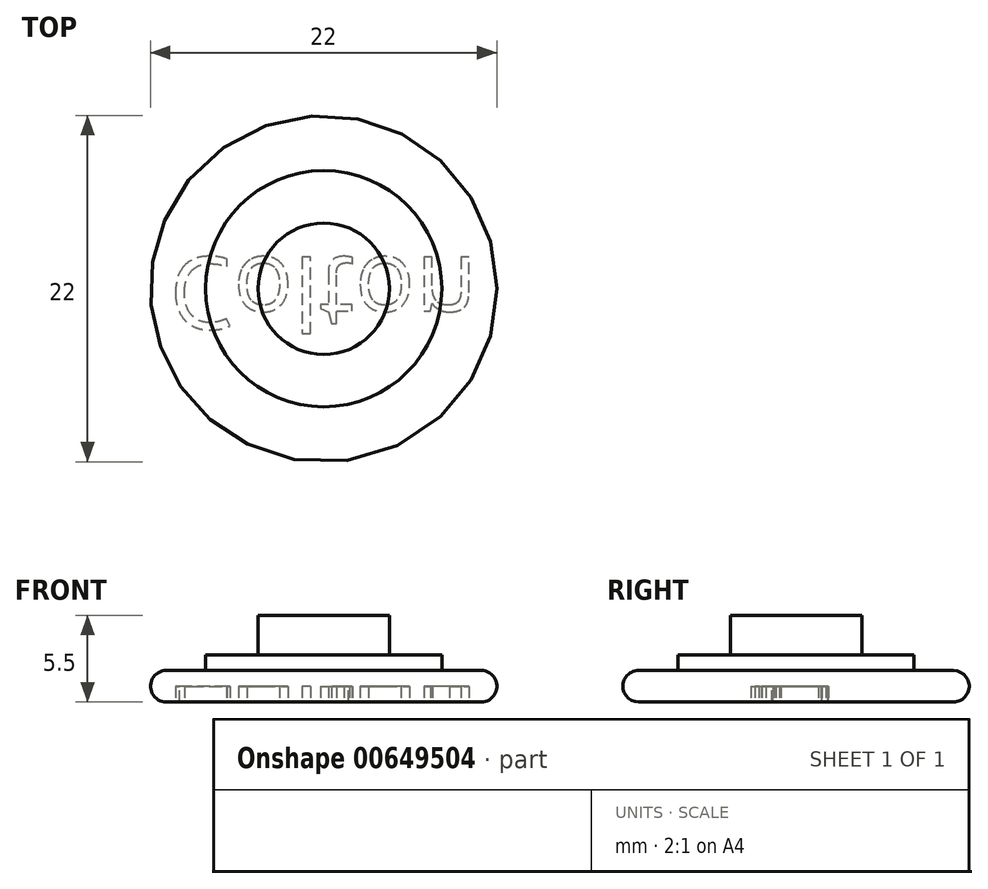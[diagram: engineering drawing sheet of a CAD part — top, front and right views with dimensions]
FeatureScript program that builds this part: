
annotation { "Feature Type Name" : "Feature", "Feature Type Description" : "" }
export const myFeature = defineFeature(function(context is Context, id is Id, definition is map)
    precondition{}
    {
        {
            var Q0;
            Q0=qCreatedBy(makeId("Top.planeOp"),FACE);
            var sketch = newSketch(context, id + "F0", { "sketchPlane" : qUnion([Q0])});
            skCircle(sketch, "E0", {"center": v(0, 0) * mm, "radius": 11 * mm});
            skCircle(sketch, "E1", {"center": v(0, 0) * mm, "radius": 7.5 * mm});
            skCircle(sketch, "E2", {"center": v(0, 0) * mm, "radius": 4.17 * mm});
            skSolve(sketch);
        }
        {
            var Q0;
            Q0=makeQuery(id+"F0.imprint","IMPRINT",FACE,{"disambiguationData":[TD([[makeQuery(id+"F0.imprint","IMPRINT",EDGE,{"derivedFrom":sQuery(id+"F0.wireOp",EDGE,"E0")}),1.0]])]});
            extrude(context, id + "F1", {"entities" : qUnion([Q0]), "depth" : 2 * mm, "offsetDistance" : 25 * mm});
        }
        {
            var Q0;
            Q0=makeQuery(id+"F0.imprint","IMPRINT",FACE,{"disambiguationData":[TD([[makeQuery(id+"F0.imprint","IMPRINT",EDGE,{"derivedFrom":sQuery(id+"F0.wireOp",EDGE,"E1")}),1.0]])]});
            extrude(context, id + "F2", {"entities" : qUnion([Q0]), "operationType" : NewBodyOperationType.ADD, "depth" : 3 * mm, "offsetDistance" : 25 * mm});
        }
        {
            var Q0;
            Q0=makeQuery(id+"F0.imprint","IMPRINT",FACE,{"disambiguationData":[TD([[makeQuery(id+"F0.imprint","IMPRINT",EDGE,{"derivedFrom":sQuery(id+"F0.wireOp",EDGE,"E2")}),1.0]])]});
            extrude(context, id + "F3", {"entities" : qUnion([Q0]), "operationType" : NewBodyOperationType.ADD, "depth" : 5.5 * mm, "offsetDistance" : 25 * mm});
        }
        {
            var Q0;
            Q0=makeQuery(id+"F1.opExtrude","CAP_EDGE",EDGE,{"disambiguationData":[OSD([sQuery(id+"F0.wireOp",EDGE,"E0")])],"isStart":false});
            var Q1;
            Q1=makeQuery(id+"F1.opExtrude","CAP_EDGE",EDGE,{"disambiguationData":[OSD([sQuery(id+"F0.wireOp",EDGE,"E0")])],"isStart":true});
            fillet(context, id + "F4", {"entities" : qUnion([Q0, Q1]), "radius" : 1 * mm, "tangentPropagation" : true, "allowEdgeOverflow" : false});
        }
        {
            var Q0;
            {var subQ0=sQuery(id+"F0.wireOp",EDGE,"E2");var subQ1=sQuery(id+"F0.wireOp",EDGE,"E1");Q0=makeQuery(id+"F3.boolean.opBoolean","MERGE",FACE,{"derivedFrom":[makeQuery(id+"F2.boolean.opBoolean","MERGE",FACE,{"derivedFrom":[makeQuery(id+"F1.opExtrude","CAP_FACE",FACE,{"disambiguationData":[OSD([sQuery(id+"F0.wireOp",EDGE,"E0"),subQ1])],"isStart":true}),makeQuery(id+"F2.opExtrude","CAP_FACE",FACE,{"disambiguationData":[OSD([subQ1,subQ0])],"isStart":true})]}),makeQuery(id+"F3.opExtrude","CAP_FACE",FACE,{"disambiguationData":[OSD([subQ0])],"isStart":true})]});}
            var sketch = newSketch(context, id + "F5", { "sketchPlane" : qUnion([Q0])});
            skText(sketch, "E3", { "text": "Colton", "fontName": "OpenSans-Regular.ttf"});
            const initialGuessF5  = {"E3": [-0.0098, -0.002, 1, 0, 0.0046]};
            skSetInitialGuess(sketch, initialGuessF5);
            skSolve(sketch);
        }
        {
            var Q0;
            Q0 = qSketchRegion(id + "F5", true);
            extrude(context, id + "F6", {"entities" : qUnion([Q0]), "operationType" : NewBodyOperationType.REMOVE, "oppositeDirection" : true, "depth" : 1 * mm, "offsetDistance" : 25 * mm});
        }
    });
